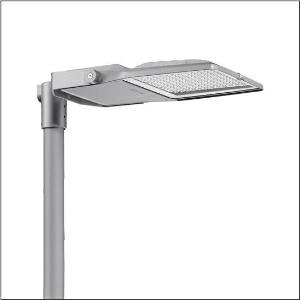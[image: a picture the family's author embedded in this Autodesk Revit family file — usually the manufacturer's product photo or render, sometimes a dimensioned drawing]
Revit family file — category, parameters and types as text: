
# Revit family: floodlight_fl_21_iq_midi___pl52_5xa7782e4d3a_8c54
name_source: partatom
category: Lighting Fixtures
units: mm (PartAtom-declared; Revit-internal decimal feet)

## family parameters
Cut with Voids When Loaded = No
Host = Face
Light Source = No
Part Type = Normal
Room Calculation Point = No
Round Connector Dimension = Use Diameter
Shared = No

## types (1)
- --- (1 x LED, 28010 lm, 208.1 W, 4000K)
    Apparent Load = 208 VA
    CIE Flux Codes = 26 60 98 100 100
    Color Rendering = 70
    Color Temperature = 4000K
    Default Elevation = 1800 mm
    Description = Floodlight FL 21 iQ midi, floodlight, primary light control with lens, of PMMA, primary optical cover: protective disc, of toughened safety glass, transparent, light distribution: PL52, light emission: direct distribution, installation type: surface-mounted, LED, High Power LED, rated luminous flux: 28.010lm, luminous efficacy: 135lm/W, light colour: 740, colour temperature: 4000K, control gear: ECG iQ, control: optimised constant luminous flux control (CLO 2.0), Desk-Remote (wireless, voltage-free reading and setting of iQ features in the workshop via application-optimized NFC function/RFID function), Smart-Wire, Night-Set, Temp-Guard, Auto-Match, Street-Remote, with terminal, 6-pole, mains connection: 220..240V, AC, 50/60Hz, start of lifetime: 208W, end of service life: 227W, reduction: 90W, luminaire housing, of diecast aluminium, powder-coated, Siteco® metallic grey (DB 702S), corrosivity category C5 mid according to DIN EN ISO 12944, sealing non-destructively replaceable, please order mast flange separately, mast bracket, of steel, galvanised, powder-coated, Siteco® metallic grey (DB 702S), protection rating (complete): IP66, insulation class (complete): insulation class II (safety insulation), certification: CE, protection symbol: D, impact resistance: IK08, permissible operating ambient temperature: -40..+40°C, permissible operating ambient temperature for outdoor applications: -40..+50°C, standard: DIN EN 12944, LABS conformity tested according to VDMA 24364:2018-05, packaging unit: 1 piece

Light Distribution: PL52
    Height = 76 mm
    Lamp = 1 x LED
    Lamp Light Flux = 28010 lm
    Lamp Power = 208.1 W
    Lamp count = 1
    Length = 657 mm
    Luminous efficacy = 135 lm/W
    Manufacturer = Siteco
    ModVariant = No
    Model = 5XA7782E4D3A
    Number of Poles = 1
    OnlyDefault = Yes
    Power Factor = 1
    Product Name = Floodlight FL 21 iQ midi | PL52
    Product group = floodlight | pylon annexe
    ProductGroupID = 6200
    Protection Class = Protection class II
    Protection Degree = IP 66
    RLX_Detail_Level = 1
    RLX_Emergency_Light_Flux = 0 lm
    RLX_Emergency_Type = 0
    RLX_Emergency_Type_DB = No
    RlxData = <blob elided: 153853 chars, md5=ddea27f4>
    Socket = socket
    Standby Power = 0 W
    System Light Flux = 28010 lm
    System Power = 208 W
    Type Comments = factory setting: luminous flux: 100 % | dim-lin: 254 | 710 mA
    Type Image = l_1007123.jpg
    URL = http://relux.com
    VarID = @adj_036099
    Voltage = 0 V
    Weight = 0.00 kg
    Width = 442 mm

## geometry (parser evidence)
native form markers: Blend x4, Sweep x11
no freeform markers — native parametric forms only
